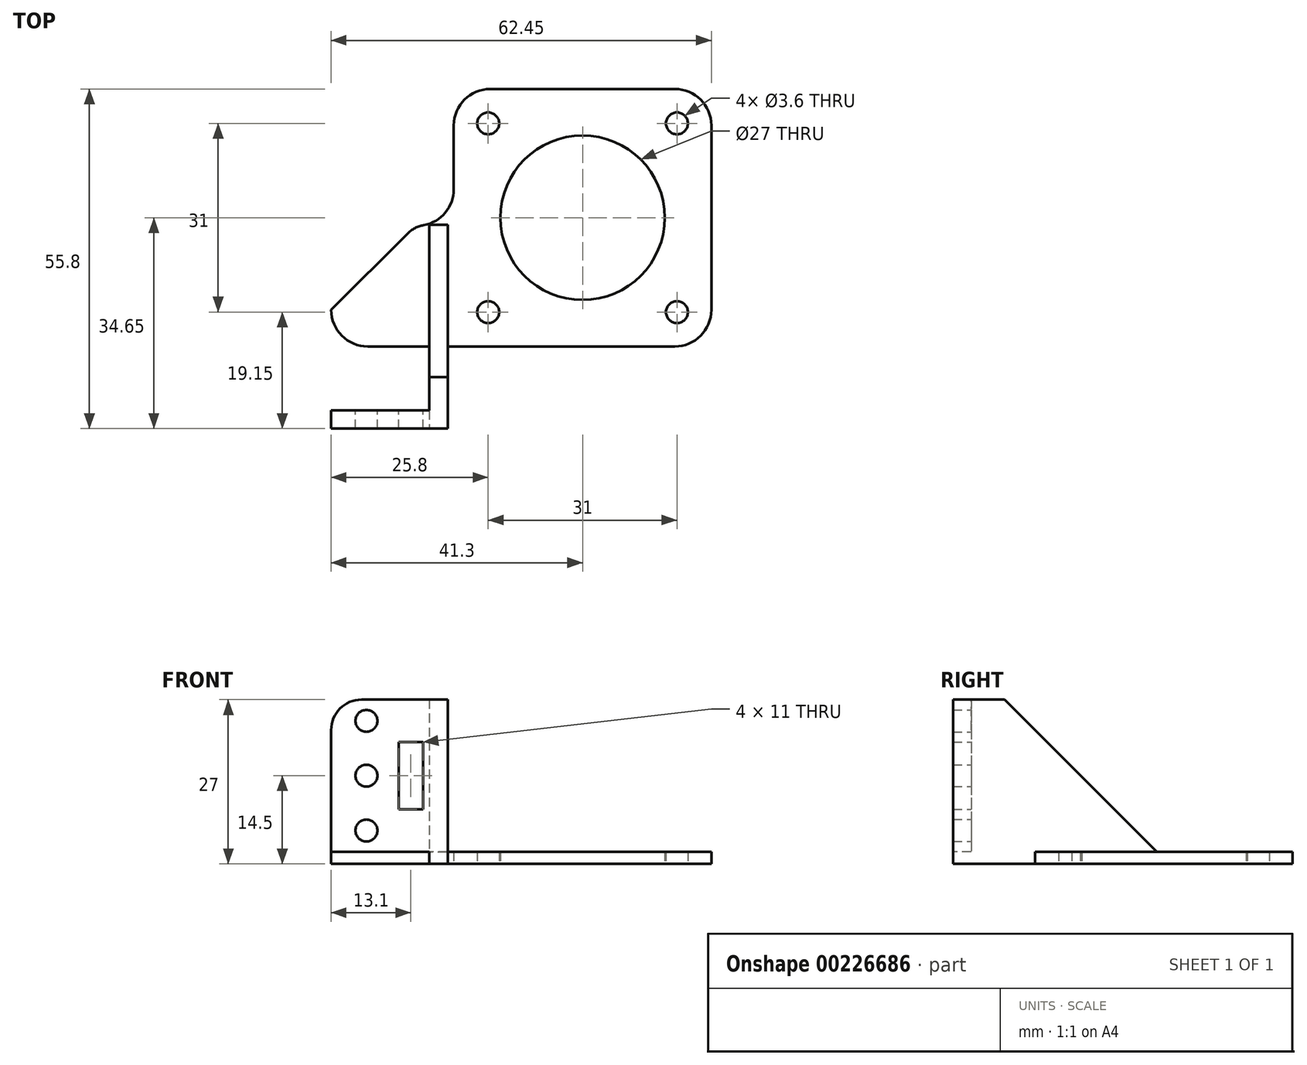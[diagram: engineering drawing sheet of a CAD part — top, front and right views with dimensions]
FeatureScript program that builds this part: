
annotation { "Feature Type Name" : "Feature", "Feature Type Description" : "" }
export const myFeature = defineFeature(function(context is Context, id is Id, definition is map)
    precondition{}
    {
        {
            var Q0;
            Q0=qCreatedBy(makeId("Top.planeOp"),FACE);
            var sketch = newSketch(context, id + "F0", { "sketchPlane" : qUnion([Q0])});
            skLineSegment(sketch, "E0.bottom", {"start": v(21.15, 21.15) * mm, "end": v(-21.15, 21.15) * mm});
            skLineSegment(sketch, "E0.top", {"start": v(21.15, -21.15) * mm, "end": v(-21.15, -21.15) * mm});
            skLineSegment(sketch, "E0.left", {"start": v(21.15, 21.15) * mm, "end": v(21.15, -21.15) * mm});
            skLineSegment(sketch, "E0.right", {"start": v(-21.15, 21.15) * mm, "end": v(-21.15, -21.15) * mm});
            skPoint(sketch, "E0.middle", {"position": v(0, 0) * mm});
            skLineSegment(sketch, "E1.bottom", {"start": v(15.5, 15.5) * mm, "end": v(-15.5, 15.5) * mm, "construction": true});
            skLineSegment(sketch, "E1.top", {"start": v(15.5, -15.5) * mm, "end": v(-15.5, -15.5) * mm, "construction": true});
            skLineSegment(sketch, "E1.left", {"start": v(15.5, 15.5) * mm, "end": v(15.5, -15.5) * mm, "construction": true});
            skLineSegment(sketch, "E1.right", {"start": v(-15.5, 15.5) * mm, "end": v(-15.5, -15.5) * mm, "construction": true});
            skCircle(sketch, "E2", {"center": v(-15.5, 15.5) * mm, "radius": 1.8 * mm});
            skCircle(sketch, "E3", {"center": v(15.5, 15.5) * mm, "radius": 1.8 * mm});
            skCircle(sketch, "E4", {"center": v(15.5, -15.5) * mm, "radius": 1.8 * mm});
            skCircle(sketch, "E5", {"center": v(-15.5, -15.5) * mm, "radius": 1.8 * mm});
            skCircle(sketch, "E6", {"center": v(0, 0) * mm, "radius": 13.5 * mm});
            skLineSegment(sketch, "E7.bottom", {"start": v(-21.15, -21.15) * mm, "end": v(-41.3, -21.15) * mm});
            skLineSegment(sketch, "E7.top", {"start": v(-21.15, -1.15) * mm, "end": v(-41.3, -1.15) * mm});
            skLineSegment(sketch, "E7.left", {"start": v(-21.15, -21.15) * mm, "end": v(-21.15, -1.15) * mm});
            skLineSegment(sketch, "E7.right", {"start": v(-41.3, -21.15) * mm, "end": v(-41.3, -1.15) * mm});
            skLineSegment(sketch, "E8.bottom", {"start": v(-41.3, -21.15) * mm, "end": v(-21.16, -21.15) * mm});
            skLineSegment(sketch, "E8.top", {"start": v(-41.3, -34.65) * mm, "end": v(-21.16, -34.65) * mm});
            skLineSegment(sketch, "E8.left", {"start": v(-41.3, -21.15) * mm, "end": v(-41.3, -34.65) * mm});
            skLineSegment(sketch, "E8.right", {"start": v(-21.16, -21.15) * mm, "end": v(-21.16, -34.65) * mm});
            skSolve(sketch);
        }
        {
            var Q0;
            Q0=makeQuery(id+"F0.imprint","IMPRINT",FACE,{"disambiguationData":[TD([[makeQuery(id+"F0.imprint","IMPRINT",EDGE,{"derivedFrom":sQuery(id+"F0.wireOp",EDGE,"E0.bottom")}),1.0]])]});
            var Q1;
            Q1=makeQuery(id+"F0.imprint","IMPRINT",FACE,{"disambiguationData":[TD([[makeQuery(id+"F0.imprint","IMPRINT",EDGE,{"derivedFrom":sQuery(id+"F0.wireOp",EDGE,"E7.bottom")}),-1.0]])]});
            var Q2;
            Q2=makeQuery(id+"F0.imprint","IMPRINT",FACE,{"disambiguationData":[TD([[makeQuery(id+"F0.imprint","IMPRINT",EDGE,{"derivedFrom":sQuery(id+"F0.wireOp",EDGE,"E8.bottom")}),-1.0]])]});
            extrude(context, id + "F1", {"entities" : qUnion([Q0, Q1, Q2]), "depth" : 2 * mm});
        }
        {
            var Q0;
            Q0=qCreatedBy(makeId("Top.planeOp"),FACE);
            var sketch = newSketch(context, id + "F2", { "sketchPlane" : qUnion([Q0])});
            skLineSegment(sketch, "E9.bottom", {"start": v(-22.16, -1.15) * mm, "end": v(-25.16, -1.15) * mm});
            skLineSegment(sketch, "E9.top", {"start": v(-22.16, -34.65) * mm, "end": v(-25.16, -34.65) * mm});
            skLineSegment(sketch, "E9.left", {"start": v(-22.16, -1.15) * mm, "end": v(-22.16, -34.65) * mm});
            skLineSegment(sketch, "E9.right", {"start": v(-25.16, -1.15) * mm, "end": v(-25.16, -34.65) * mm});
            skSolve(sketch);
        }
        {
            var Q0;
            Q0 = qSketchRegion(id + "F2", true);
            extrude(context, id + "F3", {"entities" : qUnion([Q0]), "operationType" : NewBodyOperationType.ADD, "depth" : 27 * mm});
        }
        {
            var Q0;
            {var subQ0=sQuery(id+"F0.wireOp",EDGE,"E8.left");var subQ1=sQuery(id+"F0.wireOp",EDGE,"E7.right");var subQ2=sQuery(id+"F0.wireOp",EDGE,"E8.top");var subQ3=sQuery(id+"F0.wireOp",EDGE,"E7.top");Q0=makeQuery(id+"F3.boolean.opBoolean","SPLIT",FACE,{"disambiguationData":[TD([makeQuery(id+"F3.opExtrude","SWEPT_FACE",FACE,{"disambiguationData":[OSD([sQuery(id+"F2.wireOp",EDGE,"E9.right")])]})])],"derivedFrom":makeQuery(id+"F1.opExtrude","CAP_FACE",FACE,{"disambiguationData":[OSD([sQuery(id+"F0.wireOp",EDGE,"E0.bottom"),sQuery(id+"F0.wireOp",EDGE,"E0.top"),sQuery(id+"F0.wireOp",EDGE,"E0.left"),sQuery(id+"F0.wireOp",EDGE,"E0.right"),sQuery(id+"F0.wireOp",EDGE,"E2"),sQuery(id+"F0.wireOp",EDGE,"E3"),sQuery(id+"F0.wireOp",EDGE,"E4"),sQuery(id+"F0.wireOp",EDGE,"E5"),sQuery(id+"F0.wireOp",EDGE,"E6"),sQuery(id+"F0.wireOp",EDGE,"E7.bottom"),subQ3,subQ1,subQ2,subQ0,sQuery(id+"F0.wireOp",EDGE,"E8.right")])],"isStart":false})});}
            var sketch = newSketch(context, id + "F4", { "sketchPlane" : qUnion([Q0])});
            skLineSegment(sketch, "E10.bottom", {"start": v(-41.3, -31.65) * mm, "end": v(-25.16, -31.65) * mm});
            skLineSegment(sketch, "E10.top", {"start": v(-41.3, -34.65) * mm, "end": v(-25.16, -34.65) * mm});
            skLineSegment(sketch, "E10.left", {"start": v(-41.3, -31.65) * mm, "end": v(-41.3, -34.65) * mm});
            skLineSegment(sketch, "E10.right", {"start": v(-25.16, -31.65) * mm, "end": v(-25.16, -34.65) * mm});
            skSolve(sketch);
        }
        {
            var Q0;
            Q0=makeQuery(id+"F4.imprint","IMPRINT",FACE,{"disambiguationData":[TD([[makeQuery(id+"F4.imprint","IMPRINT",EDGE,{"derivedFrom":sQuery(id+"F4.wireOp",EDGE,"E10.bottom")}),-1.0]])]});
            extrude(context, id + "F5", {"entities" : qUnion([Q0]), "operationType" : NewBodyOperationType.ADD, "depth" : 25 * mm});
        }
        {
            var Q0;
            Q0=makeQuery(id+"F5.opExtrude","SWEPT_FACE",FACE,{"disambiguationData":[OSD([sQuery(id+"F4.wireOp",EDGE,"E10.bottom")])]});
            var sketch = newSketch(context, id + "F6", { "sketchPlane" : qUnion([Q0])});
            skCircle(sketch, "E11", {"center": v(35.5, 14.5) * mm, "radius": 1.8 * mm});
            skCircle(sketch, "E12", {"center": v(35.5, 5.5) * mm, "radius": 1.8 * mm});
            skCircle(sketch, "E13", {"center": v(35.5, 23.5) * mm, "radius": 1.8 * mm});
            skLineSegment(sketch, "E14.bottom", {"start": v(30.2, 20) * mm, "end": v(26.2, 20) * mm});
            skLineSegment(sketch, "E14.top", {"start": v(30.2, 9) * mm, "end": v(26.2, 9) * mm});
            skLineSegment(sketch, "E14.left", {"start": v(30.2, 20) * mm, "end": v(30.2, 9) * mm});
            skLineSegment(sketch, "E14.right", {"start": v(26.2, 20) * mm, "end": v(26.2, 9) * mm});
            skSolve(sketch);
        }
        {
            var Q0;
            Q0=makeQuery(id+"F6.imprint","IMPRINT",FACE,{"disambiguationData":[TD([[makeQuery(id+"F6.imprint","IMPRINT",EDGE,{"derivedFrom":sQuery(id+"F6.wireOp",EDGE,"E11")}),1.0]])]});
            var Q1;
            Q1=makeQuery(id+"F6.imprint","IMPRINT",FACE,{"disambiguationData":[TD([[makeQuery(id+"F6.imprint","IMPRINT",EDGE,{"derivedFrom":sQuery(id+"F6.wireOp",EDGE,"E12")}),1.0]])]});
            var Q2;
            Q2=makeQuery(id+"F6.imprint","IMPRINT",FACE,{"disambiguationData":[TD([[makeQuery(id+"F6.imprint","IMPRINT",EDGE,{"derivedFrom":sQuery(id+"F6.wireOp",EDGE,"E13")}),1.0]])]});
            var Q3;
            Q3=makeQuery(id+"F6.imprint","IMPRINT",FACE,{"disambiguationData":[TD([[makeQuery(id+"F6.imprint","IMPRINT",EDGE,{"derivedFrom":sQuery(id+"F6.wireOp",EDGE,"E14.bottom")}),1.0]])]});
            extrude(context, id + "F7", {"entities" : qUnion([Q0, Q1, Q2, Q3]), "operationType" : NewBodyOperationType.REMOVE, "oppositeDirection" : true, "depth" : 25 * mm});
        }
        {
            var Q0;
            Q0=makeQuery(id+"F3.opExtrude","CAP_EDGE",EDGE,{"disambiguationData":[OSD([sQuery(id+"F2.wireOp",EDGE,"E9.bottom")])],"isStart":false});
            chamfer(context, id + "F8", {"entities" : qUnion([Q0]), "width" : 25 * mm, "tangentPropagation" : true});
        }
        {
            var Q0;
            Q0=makeQuery(id+"F1.opExtrude","SWEPT_EDGE",EDGE,{"disambiguationData":[OSD([sQuery(id+"F0.wireOp",EDGE,"E7.top"),sQuery(id+"F0.wireOp",EDGE,"E7.right")])]});
            chamfer(context, id + "F9", {"entities" : qUnion([Q0]), "width" : 14 * mm, "tangentPropagation" : true});
        }
        {
            var Q0;
            {var subQ0=sQuery(id+"F0.wireOp",EDGE,"E7.right");Q0=makeQuery(id+"F9.opChamfer","BLEND_EDGE",EDGE,{"blendedFrom":[makeQuery(id+"F1.opExtrude","SWEPT_EDGE",EDGE,{"disambiguationData":[OSD([sQuery(id+"F0.wireOp",EDGE,"E7.top"),subQ0])]}),makeQuery(id+"F5.boolean.opBoolean","MERGE",FACE,{"derivedFrom":[makeQuery(id+"F1.opExtrude","SWEPT_FACE",FACE,{"disambiguationData":[OSD([subQ0,sQuery(id+"F0.wireOp",EDGE,"E8.left")])]}),makeQuery(id+"F5.opExtrude","SWEPT_FACE",FACE,{"disambiguationData":[OSD([sQuery(id+"F4.wireOp",EDGE,"E10.left")])]})]})],"blendedInto":[makeQuery(id+"F5.boolean.opBoolean","MERGE",FACE,{"derivedFrom":[makeQuery(id+"F1.opExtrude","SWEPT_FACE",FACE,{"disambiguationData":[OSD([subQ0,sQuery(id+"F0.wireOp",EDGE,"E8.left")])]}),makeQuery(id+"F5.opExtrude","SWEPT_FACE",FACE,{"disambiguationData":[OSD([sQuery(id+"F4.wireOp",EDGE,"E10.left")])]})]})]});}
            var Q1;
            {var subQ0=sQuery(id+"F0.wireOp",EDGE,"E7.top");Q1=makeQuery(id+"F9.opChamfer","BLEND_EDGE",EDGE,{"blendedFrom":[makeQuery(id+"F1.opExtrude","SWEPT_EDGE",EDGE,{"disambiguationData":[OSD([subQ0,sQuery(id+"F0.wireOp",EDGE,"E7.right")])]}),makeQuery(id+"F3.boolean.opBoolean","MERGE",FACE,{"derivedFrom":[makeQuery(id+"F1.opExtrude","SWEPT_FACE",FACE,{"disambiguationData":[OSD([subQ0])]}),makeQuery(id+"F3.opExtrude","SWEPT_FACE",FACE,{"disambiguationData":[OSD([sQuery(id+"F2.wireOp",EDGE,"E9.bottom")])]})]})],"blendedInto":[makeQuery(id+"F3.boolean.opBoolean","MERGE",FACE,{"derivedFrom":[makeQuery(id+"F1.opExtrude","SWEPT_FACE",FACE,{"disambiguationData":[OSD([subQ0])]}),makeQuery(id+"F3.opExtrude","SWEPT_FACE",FACE,{"disambiguationData":[OSD([sQuery(id+"F2.wireOp",EDGE,"E9.bottom")])]})]})]});}
            var Q2;
            Q2=makeQuery(id+"F1.opExtrude","SWEPT_EDGE",EDGE,{"disambiguationData":[OSD([sQuery(id+"F0.wireOp",EDGE,"E8.top"),sQuery(id+"F0.wireOp",EDGE,"E8.right")])]});
            var Q3;
            Q3=makeQuery(id+"F5.opExtrude","CAP_EDGE",EDGE,{"disambiguationData":[OSD([sQuery(id+"F4.wireOp",EDGE,"E10.left")])],"isStart":false});
            fillet(context, id + "F10", {"entities" : qUnion([Q0, Q1, Q2, Q3]), "radius" : 5 * mm, "tangentPropagation" : true, "allowEdgeOverflow" : false});
        }
        {
            var Q0;
            Q0=makeQuery(id+"F1.opExtrude","SWEPT_EDGE",EDGE,{"disambiguationData":[OSD([sQuery(id+"F0.wireOp",EDGE,"E0.top"),sQuery(id+"F0.wireOp",EDGE,"E0.left")])]});
            var Q1;
            Q1=makeQuery(id+"F1.opExtrude","SWEPT_EDGE",EDGE,{"disambiguationData":[OSD([sQuery(id+"F0.wireOp",EDGE,"E0.bottom"),sQuery(id+"F0.wireOp",EDGE,"E0.left")])]});
            var Q2;
            Q2=makeQuery(id+"F1.opExtrude","SWEPT_EDGE",EDGE,{"disambiguationData":[OSD([sQuery(id+"F0.wireOp",EDGE,"E0.bottom"),sQuery(id+"F0.wireOp",EDGE,"E0.right")])]});
            var Q3;
            Q3=makeQuery(id+"F1.opExtrude","SWEPT_EDGE",EDGE,{"disambiguationData":[OSD([sQuery(id+"F0.wireOp",EDGE,"E0.right"),sQuery(id+"F0.wireOp",EDGE,"E7.top"),sQuery(id+"F0.wireOp",EDGE,"E7.left")])]});
            var Q4;
            Q4=makeQuery(id+"F1.opExtrude","SWEPT_EDGE",EDGE,{"disambiguationData":[OSD([sQuery(id+"F0.wireOp",EDGE,"E7.bottom"),sQuery(id+"F0.wireOp",EDGE,"E8.bottom"),sQuery(id+"F0.wireOp",EDGE,"E8.right")])]});
            fillet(context, id + "F11", {"entities" : qUnion([Q0, Q1, Q2, Q3, Q4]), "radius" : 6 * mm, "tangentPropagation" : true, "allowEdgeOverflow" : false});
        }
    });
